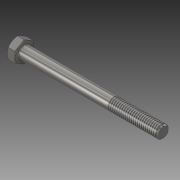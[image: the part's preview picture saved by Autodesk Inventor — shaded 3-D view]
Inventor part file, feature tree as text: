
AUTODESK INVENTOR PART (.ipt)
format: ipt  version: 2018 (Build 220112000, 112)  size: 123,904 bytes
history: native  units: in
note: dims shown in document units (in); Inventor stores cm internally (conversion verified against a paired STEP export)
features: thread x1, other x1
ambient origin geometry x8: Origin, YZ Plane, XZ Plane, XY Plane, X Axis, Y Axis, Z Axis, Center Point
bodies: Solid1 (feature_tree)
feature tree (2):
  thread  "Thread1"  [1 undecoded]
  other  "HeadFillet"
note: 1 required parameter value undecoded (feature->parameter linkage not recoverable at this tier; creation-order binding heuristic only, values carry confidence <= 0.55)
